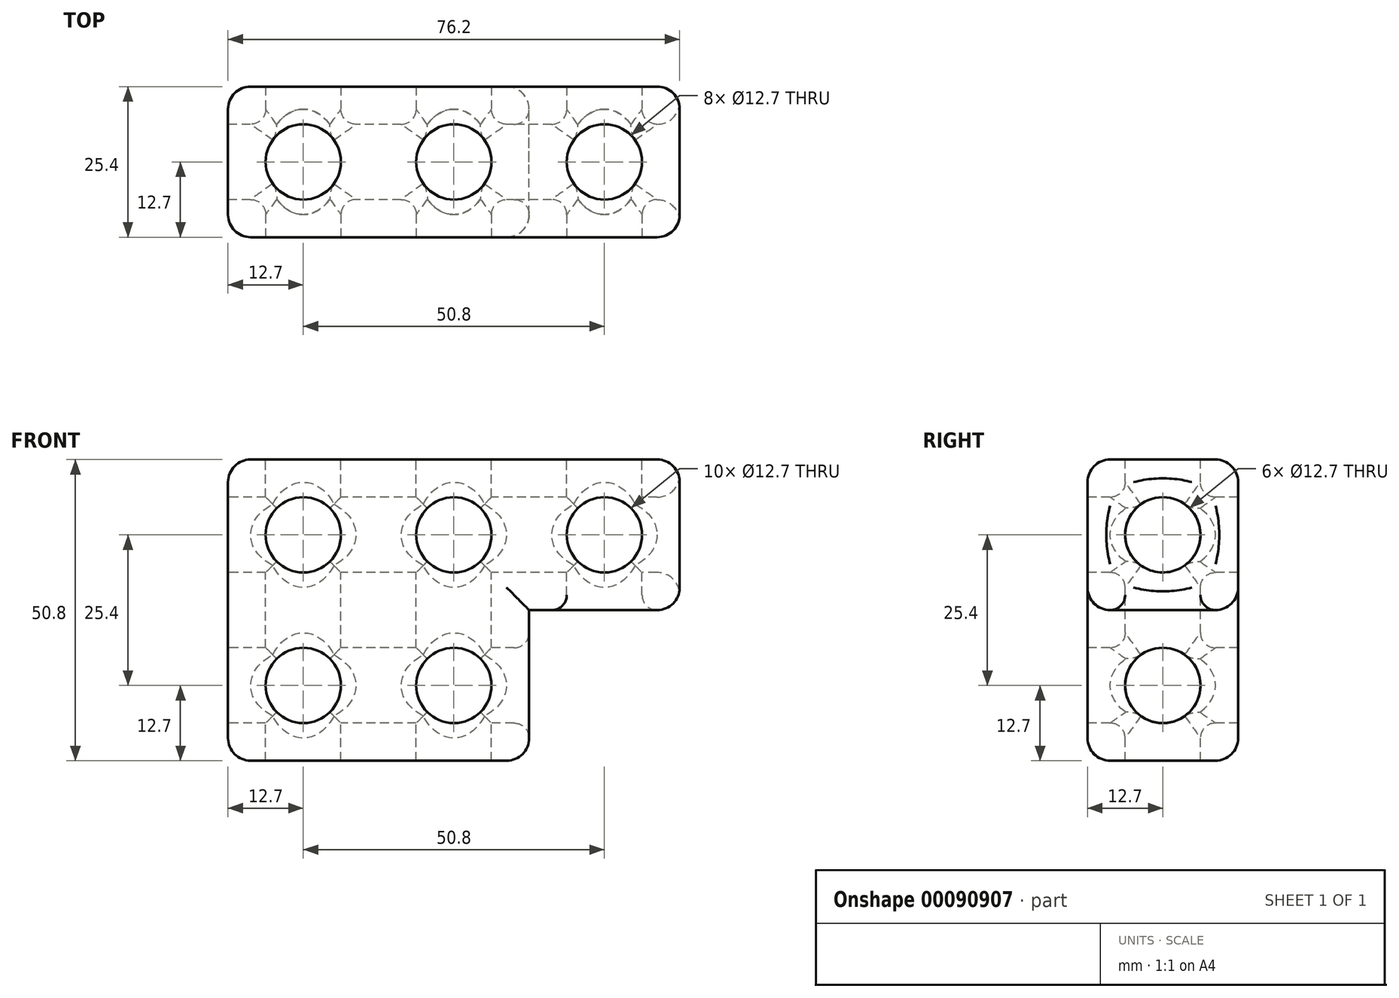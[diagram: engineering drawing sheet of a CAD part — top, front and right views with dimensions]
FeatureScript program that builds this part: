
annotation { "Feature Type Name" : "Feature", "Feature Type Description" : "" }
export const myFeature = defineFeature(function(context is Context, id is Id, definition is map)
    precondition{}
    {
        {
            var Q0;
            Q0=qCreatedBy(makeId("Top.planeOp"),FACE);
            var sketch = newSketch(context, id + "F0", { "sketchPlane" : qUnion([Q0])});
            skLineSegment(sketch, "E0.top", {"start": v(0, 25.4) * mm, "end": v(50.8, 25.4) * mm});
            skLineSegment(sketch, "E0.left", {"start": v(0, 0) * mm, "end": v(0, 25.4) * mm});
            skLineSegment(sketch, "E0.right", {"start": v(50.8, 0) * mm, "end": v(50.8, 25.4) * mm});
            skLineSegment(sketch, "E1", {"start": v(0, 0) * mm, "end": v(50.8, 0) * mm});
            skSolve(sketch);
        }
        {
            var Q0;
            Q0 = qSketchRegion(id + "F0", true);
            extrude(context, id + "F1", {"entities" : qUnion([Q0]), "depth" : 25.4 * mm});
        }
        {
            var Q0;
            Q0=makeQuery(id+"F1.opExtrude","CAP_FACE",FACE,{"disambiguationData":[OSD([sQuery(id+"F0.wireOp",EDGE,"E0.top"),sQuery(id+"F0.wireOp",EDGE,"E0.left"),sQuery(id+"F0.wireOp",EDGE,"E0.right"),sQuery(id+"F0.wireOp",EDGE,"E1")])],"isStart":false});
            var sketch = newSketch(context, id + "F2", { "sketchPlane" : qUnion([Q0])});
            skLineSegment(sketch, "E2.bottom", {"start": v(0, 25.4) * mm, "end": v(76.2, 25.4) * mm});
            skLineSegment(sketch, "E2.top", {"start": v(0, 0) * mm, "end": v(76.2, 0) * mm});
            skLineSegment(sketch, "E2.left", {"start": v(0, 25.4) * mm, "end": v(0, 0) * mm});
            skLineSegment(sketch, "E2.right", {"start": v(76.2, 25.4) * mm, "end": v(76.2, 0) * mm});
            skSolve(sketch);
        }
        {
            var Q0;
            Q0 = qSketchRegion(id + "F2", true);
            extrude(context, id + "F3", {"entities" : qUnion([Q0]), "operationType" : NewBodyOperationType.ADD, "depth" : 25.4 * mm});
        }
        {
            var Q0;
            Q0=makeQuery(id+"F3.boolean.opBoolean","MERGE",FACE,{"derivedFrom":[makeQuery(id+"F1.opExtrude","SWEPT_FACE",FACE,{"disambiguationData":[OSD([sQuery(id+"F0.wireOp",EDGE,"E1")])]}),makeQuery(id+"F3.opExtrude","SWEPT_FACE",FACE,{"disambiguationData":[OSD([sQuery(id+"F2.wireOp",EDGE,"E2.top")])]})]});
            var sketch = newSketch(context, id + "F4", { "sketchPlane" : qUnion([Q0])});
            skCircle(sketch, "E3", {"center": v(12.7, 38.1) * mm, "radius": 6.35 * mm});
            skCircle(sketch, "E4", {"center": v(38.1, 38.1) * mm, "radius": 6.35 * mm});
            skCircle(sketch, "E5", {"center": v(63.5, 38.1) * mm, "radius": 6.35 * mm});
            skCircle(sketch, "E6", {"center": v(38.1, 12.7) * mm, "radius": 6.35 * mm});
            skCircle(sketch, "E7", {"center": v(12.7, 12.7) * mm, "radius": 6.35 * mm});
            skSolve(sketch);
        }
        {
            var Q0;
            Q0 = qSketchRegion(id + "F4", true);
            extrude(context, id + "F5", {"entities" : qUnion([Q0]), "operationType" : NewBodyOperationType.REMOVE, "oppositeDirection" : true, "depth" : 25.4 * mm});
        }
        {
            var Q0;
            Q0=makeQuery(id+"F3.opExtrude","CAP_FACE",FACE,{"disambiguationData":[OSD([sQuery(id+"F2.wireOp",EDGE,"E2.bottom"),sQuery(id+"F2.wireOp",EDGE,"E2.top"),sQuery(id+"F2.wireOp",EDGE,"E2.left"),sQuery(id+"F2.wireOp",EDGE,"E2.right")])],"isStart":false});
            var sketch = newSketch(context, id + "F6", { "sketchPlane" : qUnion([Q0])});
            skCircle(sketch, "E8", {"center": v(12.7, 12.7) * mm, "radius": 6.35 * mm});
            skPoint(sketch, "E8.centerSnap0", {"position": v(0, 12.7) * mm});
            skCircle(sketch, "E9", {"center": v(38.1, 12.7) * mm, "radius": 6.35 * mm});
            skCircle(sketch, "E10", {"center": v(63.5, 12.7) * mm, "radius": 6.35 * mm});
            skSolve(sketch);
        }
        {
            var Q0;
            Q0 = qSketchRegion(id + "F6", true);
            extrude(context, id + "F7", {"entities" : qUnion([Q0]), "operationType" : NewBodyOperationType.REMOVE, "oppositeDirection" : true, "depth" : 50.8 * mm});
        }
        {
            var Q0;
            Q0=makeQuery(id+"F3.boolean.opBoolean","MERGE",FACE,{"derivedFrom":[makeQuery(id+"F1.opExtrude","SWEPT_FACE",FACE,{"disambiguationData":[OSD([sQuery(id+"F0.wireOp",EDGE,"E0.left")])]}),makeQuery(id+"F3.opExtrude","SWEPT_FACE",FACE,{"disambiguationData":[OSD([sQuery(id+"F2.wireOp",EDGE,"E2.left")])]})]});
            var sketch = newSketch(context, id + "F8", { "sketchPlane" : qUnion([Q0])});
            skCircle(sketch, "E11", {"center": v(-12.7, 38.1) * mm, "radius": 6.35 * mm});
            skCircle(sketch, "E12", {"center": v(-12.7, 12.7) * mm, "radius": 6.35 * mm});
            skSolve(sketch);
        }
        {
            var Q0;
            Q0 = qSketchRegion(id + "F8", true);
            extrude(context, id + "F9", {"entities" : qUnion([Q0]), "operationType" : NewBodyOperationType.REMOVE, "oppositeDirection" : true, "depth" : 76.2 * mm});
        }
        {
            var Q0;
            Q0=makeQuery(id+"F7.boolean.opBoolean","COPY",EDGE,{"derivedFrom":makeQuery(id+"F7.opExtrude","CAP_EDGE",EDGE,{"disambiguationData":[OSD([sQuery(id+"F6.wireOp",EDGE,"E8")])],"isStart":false})});
            var Q1;
            Q1=makeQuery(id+"F7.boolean.opBoolean","COPY",EDGE,{"derivedFrom":makeQuery(id+"F7.opExtrude","CAP_EDGE",EDGE,{"disambiguationData":[OSD([sQuery(id+"F6.wireOp",EDGE,"E9")])],"isStart":false})});
            var Q2;
            Q2=makeQuery(id+"F5.boolean.opBoolean","COPY",EDGE,{"derivedFrom":makeQuery(id+"F5.opExtrude","CAP_EDGE",EDGE,{"disambiguationData":[OSD([sQuery(id+"F4.wireOp",EDGE,"E7")])],"isStart":false})});
            var Q3;
            Q3=makeQuery(id+"F9.boolean.opBoolean","COPY",EDGE,{"derivedFrom":makeQuery(id+"F9.opExtrude","CAP_EDGE",EDGE,{"disambiguationData":[OSD([sQuery(id+"F8.wireOp",EDGE,"E11")])],"isStart":true})});
            var Q4;
            Q4=makeQuery(id+"F9.boolean.opBoolean","COPY",EDGE,{"derivedFrom":makeQuery(id+"F9.opExtrude","CAP_EDGE",EDGE,{"disambiguationData":[OSD([sQuery(id+"F8.wireOp",EDGE,"E12")])],"isStart":true})});
            var Q5;
            Q5=makeQuery(id+"F5.boolean.opBoolean","COPY",EDGE,{"derivedFrom":makeQuery(id+"F5.opExtrude","CAP_EDGE",EDGE,{"disambiguationData":[OSD([sQuery(id+"F4.wireOp",EDGE,"E3")])],"isStart":false})});
            var Q6;
            Q6=makeQuery(id+"F5.boolean.opBoolean","COPY",EDGE,{"derivedFrom":makeQuery(id+"F5.opExtrude","CAP_EDGE",EDGE,{"disambiguationData":[OSD([sQuery(id+"F4.wireOp",EDGE,"E4")])],"isStart":false})});
            var Q7;
            Q7=makeQuery(id+"F5.boolean.opBoolean","COPY",EDGE,{"derivedFrom":makeQuery(id+"F5.opExtrude","CAP_EDGE",EDGE,{"disambiguationData":[OSD([sQuery(id+"F4.wireOp",EDGE,"E6")])],"isStart":false})});
            var Q8;
            Q8=makeQuery(id+"F5.boolean.opBoolean","COPY",EDGE,{"derivedFrom":makeQuery(id+"F5.opExtrude","CAP_EDGE",EDGE,{"disambiguationData":[OSD([sQuery(id+"F4.wireOp",EDGE,"E5")])],"isStart":false})});
            var Q9;
            Q9=makeQuery(id+"F7.boolean.opBoolean","INTERSECT",EDGE,{"derivedFrom":[makeQuery(id+"F3.opExtrude","CAP_FACE",FACE,{"disambiguationData":[OSD([sQuery(id+"F2.wireOp",EDGE,"E2.bottom"),sQuery(id+"F2.wireOp",EDGE,"E2.top"),sQuery(id+"F2.wireOp",EDGE,"E2.left"),sQuery(id+"F2.wireOp",EDGE,"E2.right")])],"isStart":true}),makeQuery(id+"F7.opExtrude","SWEPT_FACE",FACE,{"disambiguationData":[OSD([sQuery(id+"F6.wireOp",EDGE,"E10")])]})]});
            var Q10;
            Q10=makeQuery(id+"F9.boolean.opBoolean","COPY",EDGE,{"derivedFrom":makeQuery(id+"F9.opExtrude","CAP_EDGE",EDGE,{"disambiguationData":[OSD([sQuery(id+"F8.wireOp",EDGE,"E11")])],"isStart":false})});
            var Q11;
            Q11=makeQuery(id+"F9.boolean.opBoolean","INTERSECT",EDGE,{"derivedFrom":[makeQuery(id+"F1.opExtrude","SWEPT_FACE",FACE,{"disambiguationData":[OSD([sQuery(id+"F0.wireOp",EDGE,"E0.right")])]}),makeQuery(id+"F9.opExtrude","SWEPT_FACE",FACE,{"disambiguationData":[OSD([sQuery(id+"F8.wireOp",EDGE,"E12")])]})]});
            var Q12;
            Q12=makeQuery(id+"F5.boolean.opBoolean","COPY",EDGE,{"derivedFrom":makeQuery(id+"F5.opExtrude","CAP_EDGE",EDGE,{"disambiguationData":[OSD([sQuery(id+"F4.wireOp",EDGE,"E6")])],"isStart":true})});
            var Q13;
            Q13=makeQuery(id+"F5.boolean.opBoolean","COPY",EDGE,{"derivedFrom":makeQuery(id+"F5.opExtrude","CAP_EDGE",EDGE,{"disambiguationData":[OSD([sQuery(id+"F4.wireOp",EDGE,"E5")])],"isStart":true})});
            var Q14;
            Q14=makeQuery(id+"F5.boolean.opBoolean","COPY",EDGE,{"derivedFrom":makeQuery(id+"F5.opExtrude","CAP_EDGE",EDGE,{"disambiguationData":[OSD([sQuery(id+"F4.wireOp",EDGE,"E4")])],"isStart":true})});
            var Q15;
            Q15=makeQuery(id+"F5.boolean.opBoolean","COPY",EDGE,{"derivedFrom":makeQuery(id+"F5.opExtrude","CAP_EDGE",EDGE,{"disambiguationData":[OSD([sQuery(id+"F4.wireOp",EDGE,"E3")])],"isStart":true})});
            var Q16;
            Q16=makeQuery(id+"F5.boolean.opBoolean","COPY",EDGE,{"derivedFrom":makeQuery(id+"F5.opExtrude","CAP_EDGE",EDGE,{"disambiguationData":[OSD([sQuery(id+"F4.wireOp",EDGE,"E7")])],"isStart":true})});
            var Q17;
            Q17=makeQuery(id+"F7.boolean.opBoolean","COPY",EDGE,{"derivedFrom":makeQuery(id+"F7.opExtrude","CAP_EDGE",EDGE,{"disambiguationData":[OSD([sQuery(id+"F6.wireOp",EDGE,"E8")])],"isStart":true})});
            var Q18;
            Q18=makeQuery(id+"F7.boolean.opBoolean","COPY",EDGE,{"derivedFrom":makeQuery(id+"F7.opExtrude","CAP_EDGE",EDGE,{"disambiguationData":[OSD([sQuery(id+"F6.wireOp",EDGE,"E9")])],"isStart":true})});
            var Q19;
            Q19=makeQuery(id+"F7.boolean.opBoolean","COPY",EDGE,{"derivedFrom":makeQuery(id+"F7.opExtrude","CAP_EDGE",EDGE,{"disambiguationData":[OSD([sQuery(id+"F6.wireOp",EDGE,"E10")])],"isStart":true})});
            fillet(context, id + "F10", {"entities" : qUnion([Q0, Q1, Q2, Q3, Q4, Q5, Q6, Q7, Q8, Q9, Q10, Q11, Q12, Q13, Q14, Q15, Q16, Q17, Q18, Q19]), "radius" : 2.54 * mm, "tangentPropagation" : true, "allowEdgeOverflow" : false});
        }
        {
            var Q0;
            Q0=makeQuery(id+"F3.opExtrude","CAP_EDGE",EDGE,{"disambiguationData":[OSD([sQuery(id+"F2.wireOp",EDGE,"E2.right")])],"isStart":false});
            var Q1;
            Q1=makeQuery(id+"F3.opExtrude","CAP_EDGE",EDGE,{"disambiguationData":[OSD([sQuery(id+"F2.wireOp",EDGE,"E2.bottom")])],"isStart":false});
            var Q2;
            Q2=makeQuery(id+"F3.opExtrude","SWEPT_EDGE",EDGE,{"disambiguationData":[OSD([sQuery(id+"F2.wireOp",EDGE,"E2.bottom"),sQuery(id+"F2.wireOp",EDGE,"E2.right")])]});
            var Q3;
            Q3=makeQuery(id+"F3.opExtrude","CAP_EDGE",EDGE,{"disambiguationData":[OSD([sQuery(id+"F2.wireOp",EDGE,"E2.top")])],"isStart":false});
            var Q4;
            Q4=makeQuery(id+"F3.opExtrude","CAP_EDGE",EDGE,{"disambiguationData":[OSD([sQuery(id+"F2.wireOp",EDGE,"E2.top")])],"isStart":true});
            var Q5;
            Q5=makeQuery(id+"F3.opExtrude","CAP_EDGE",EDGE,{"disambiguationData":[OSD([sQuery(id+"F2.wireOp",EDGE,"E2.right")])],"isStart":true});
            var Q6;
            Q6=makeQuery(id+"F3.opExtrude","SWEPT_FACE",FACE,{"disambiguationData":[OSD([sQuery(id+"F2.wireOp",EDGE,"E2.right")])]});
            var Q7;
            Q7=makeQuery(id+"F3.opExtrude","CAP_EDGE",EDGE,{"disambiguationData":[OSD([sQuery(id+"F2.wireOp",EDGE,"E2.bottom")])],"isStart":true});
            var Q8;
            Q8=makeQuery(id+"F1.opExtrude","SWEPT_EDGE",EDGE,{"disambiguationData":[OSD([sQuery(id+"F0.wireOp",EDGE,"E0.top"),sQuery(id+"F0.wireOp",EDGE,"E0.right")])]});
            var Q9;
            Q9=makeQuery(id+"F1.opExtrude","CAP_EDGE",EDGE,{"disambiguationData":[OSD([sQuery(id+"F0.wireOp",EDGE,"E0.top")])],"isStart":true});
            var Q10;
            Q10=makeQuery(id+"F1.opExtrude","CAP_EDGE",EDGE,{"disambiguationData":[OSD([sQuery(id+"F0.wireOp",EDGE,"E0.right")])],"isStart":true});
            var Q11;
            Q11=makeQuery(id+"F1.opExtrude","CAP_EDGE",EDGE,{"disambiguationData":[OSD([sQuery(id+"F0.wireOp",EDGE,"E1")])],"isStart":true});
            var Q12;
            Q12=makeQuery(id+"F1.opExtrude","SWEPT_EDGE",EDGE,{"disambiguationData":[OSD([sQuery(id+"F0.wireOp",EDGE,"E0.right"),sQuery(id+"F0.wireOp",EDGE,"E1")])]});
            var Q13;
            Q13=makeQuery(id+"F1.opExtrude","CAP_EDGE",EDGE,{"disambiguationData":[OSD([sQuery(id+"F0.wireOp",EDGE,"E0.left")])],"isStart":true});
            var Q14;
            Q14=makeQuery(id+"F3.boolean.opBoolean","MERGE",EDGE,{"derivedFrom":[makeQuery(id+"F1.opExtrude","SWEPT_EDGE",EDGE,{"disambiguationData":[OSD([sQuery(id+"F0.wireOp",EDGE,"E0.top"),sQuery(id+"F0.wireOp",EDGE,"E0.left")])]}),makeQuery(id+"F3.opExtrude","SWEPT_EDGE",EDGE,{"disambiguationData":[OSD([sQuery(id+"F2.wireOp",EDGE,"E2.bottom"),sQuery(id+"F2.wireOp",EDGE,"E2.left")])]})]});
            var Q15;
            Q15=makeQuery(id+"F3.boolean.opBoolean","MERGE",EDGE,{"derivedFrom":[makeQuery(id+"F1.opExtrude","SWEPT_EDGE",EDGE,{"disambiguationData":[OSD([sQuery(id+"F0.wireOp",EDGE,"E0.left"),sQuery(id+"F0.wireOp",EDGE,"E1")])]}),makeQuery(id+"F3.opExtrude","SWEPT_EDGE",EDGE,{"disambiguationData":[OSD([sQuery(id+"F2.wireOp",EDGE,"E2.top"),sQuery(id+"F2.wireOp",EDGE,"E2.left")])]})]});
            var Q16;
            Q16=makeQuery(id+"F3.opExtrude","CAP_EDGE",EDGE,{"disambiguationData":[OSD([sQuery(id+"F2.wireOp",EDGE,"E2.left")])],"isStart":false});
            fillet(context, id + "F11", {"entities" : qUnion([Q0, Q1, Q2, Q3, Q4, Q5, Q6, Q7, Q8, Q9, Q10, Q11, Q12, Q13, Q14, Q15, Q16]), "radius" : 3.8 * mm, "tangentPropagation" : true, "allowEdgeOverflow" : false});
        }
        {
            var Q0;
            Q0=makeQuery(id+"F9.boolean.opBoolean","INTERSECT",EDGE,{"disambiguationData":[OD(0.0)],"derivedFrom":[makeQuery(id+"F7.boolean.opBoolean","COPY",FACE,{"disambiguationData":[OD(1.0)],"derivedFrom":makeQuery(id+"F7.opExtrude","SWEPT_FACE",FACE,{"disambiguationData":[OSD([sQuery(id+"F6.wireOp",EDGE,"E8")])]})}),makeQuery(id+"F9.opExtrude","SWEPT_FACE",FACE,{"disambiguationData":[OSD([sQuery(id+"F8.wireOp",EDGE,"E12")])]})]});
            var Q1;
            Q1=makeQuery(id+"F7.boolean.opBoolean","INTERSECT",EDGE,{"disambiguationData":[OD(0.0)],"derivedFrom":[makeQuery(id+"F5.boolean.opBoolean","COPY",FACE,{"derivedFrom":makeQuery(id+"F5.opExtrude","SWEPT_FACE",FACE,{"disambiguationData":[OSD([sQuery(id+"F4.wireOp",EDGE,"E7")])]})}),makeQuery(id+"F7.opExtrude","SWEPT_FACE",FACE,{"disambiguationData":[OSD([sQuery(id+"F6.wireOp",EDGE,"E8")])]})]});
            var Q2;
            {var subQ0=makeQuery(id+"F5.boolean.opBoolean","COPY",FACE,{"derivedFrom":makeQuery(id+"F5.opExtrude","SWEPT_FACE",FACE,{"disambiguationData":[OSD([sQuery(id+"F4.wireOp",EDGE,"E6")])]})});Q2=makeQuery(id+"F9.boolean.opBoolean","INTERSECT",EDGE,{"disambiguationData":[OD(1.0)],"derivedFrom":[makeQuery(id+"F7.boolean.opBoolean","SPLIT",FACE,{"disambiguationData":[TD([makeQuery(id+"F1.opExtrude","SWEPT_FACE",FACE,{"disambiguationData":[OSD([sQuery(id+"F0.wireOp",EDGE,"E1")])]})])],"derivedFrom":subQ0}),makeQuery(id+"F9.opExtrude","SWEPT_FACE",FACE,{"disambiguationData":[OSD([sQuery(id+"F8.wireOp",EDGE,"E12")])]})]});}
            var Q3;
            Q3=makeQuery(id+"F9.boolean.opBoolean","INTERSECT",EDGE,{"disambiguationData":[OD(1.0)],"derivedFrom":[makeQuery(id+"F7.boolean.opBoolean","COPY",FACE,{"disambiguationData":[OD(1.0)],"derivedFrom":makeQuery(id+"F7.opExtrude","SWEPT_FACE",FACE,{"disambiguationData":[OSD([sQuery(id+"F6.wireOp",EDGE,"E9")])]})}),makeQuery(id+"F9.opExtrude","SWEPT_FACE",FACE,{"disambiguationData":[OSD([sQuery(id+"F8.wireOp",EDGE,"E12")])]})]});
            var Q4;
            Q4=makeQuery(id+"F7.boolean.opBoolean","INTERSECT",EDGE,{"disambiguationData":[OD(0.0)],"derivedFrom":[makeQuery(id+"F5.boolean.opBoolean","COPY",FACE,{"derivedFrom":makeQuery(id+"F5.opExtrude","SWEPT_FACE",FACE,{"disambiguationData":[OSD([sQuery(id+"F4.wireOp",EDGE,"E6")])]})}),makeQuery(id+"F7.opExtrude","SWEPT_FACE",FACE,{"disambiguationData":[OSD([sQuery(id+"F6.wireOp",EDGE,"E9")])]})]});
            var Q5;
            {var subQ0=makeQuery(id+"F5.boolean.opBoolean","COPY",FACE,{"derivedFrom":makeQuery(id+"F5.opExtrude","SWEPT_FACE",FACE,{"disambiguationData":[OSD([sQuery(id+"F4.wireOp",EDGE,"E3")])]})});Q5=makeQuery(id+"F9.boolean.opBoolean","INTERSECT",EDGE,{"disambiguationData":[OD(0.0)],"derivedFrom":[makeQuery(id+"F7.boolean.opBoolean","SPLIT",FACE,{"disambiguationData":[TD([makeQuery(id+"F1.opExtrude","SWEPT_FACE",FACE,{"disambiguationData":[OSD([sQuery(id+"F0.wireOp",EDGE,"E1")])]})])],"derivedFrom":subQ0}),makeQuery(id+"F9.opExtrude","SWEPT_FACE",FACE,{"disambiguationData":[OSD([sQuery(id+"F8.wireOp",EDGE,"E11")])]})]});}
            var Q6;
            Q6=makeQuery(id+"F9.boolean.opBoolean","INTERSECT",EDGE,{"disambiguationData":[OD(0.0)],"derivedFrom":[makeQuery(id+"F7.boolean.opBoolean","COPY",FACE,{"disambiguationData":[OD(2.0)],"derivedFrom":makeQuery(id+"F7.opExtrude","SWEPT_FACE",FACE,{"disambiguationData":[OSD([sQuery(id+"F6.wireOp",EDGE,"E8")])]})}),makeQuery(id+"F9.opExtrude","SWEPT_FACE",FACE,{"disambiguationData":[OSD([sQuery(id+"F8.wireOp",EDGE,"E11")])]})]});
            var Q7;
            Q7=makeQuery(id+"F7.boolean.opBoolean","INTERSECT",EDGE,{"disambiguationData":[OD(1.0)],"derivedFrom":[makeQuery(id+"F5.boolean.opBoolean","COPY",FACE,{"derivedFrom":makeQuery(id+"F5.opExtrude","SWEPT_FACE",FACE,{"disambiguationData":[OSD([sQuery(id+"F4.wireOp",EDGE,"E3")])]})}),makeQuery(id+"F7.opExtrude","SWEPT_FACE",FACE,{"disambiguationData":[OSD([sQuery(id+"F6.wireOp",EDGE,"E8")])]})]});
            var Q8;
            {var subQ0=makeQuery(id+"F5.boolean.opBoolean","COPY",FACE,{"derivedFrom":makeQuery(id+"F5.opExtrude","SWEPT_FACE",FACE,{"disambiguationData":[OSD([sQuery(id+"F4.wireOp",EDGE,"E4")])]})});Q8=makeQuery(id+"F9.boolean.opBoolean","INTERSECT",EDGE,{"disambiguationData":[OD(0.0)],"derivedFrom":[makeQuery(id+"F7.boolean.opBoolean","SPLIT",FACE,{"disambiguationData":[TD([makeQuery(id+"F1.opExtrude","SWEPT_FACE",FACE,{"disambiguationData":[OSD([sQuery(id+"F0.wireOp",EDGE,"E1")])]})])],"derivedFrom":subQ0}),makeQuery(id+"F9.opExtrude","SWEPT_FACE",FACE,{"disambiguationData":[OSD([sQuery(id+"F8.wireOp",EDGE,"E11")])]})]});}
            var Q9;
            Q9=makeQuery(id+"F9.boolean.opBoolean","INTERSECT",EDGE,{"disambiguationData":[OD(0.0)],"derivedFrom":[makeQuery(id+"F7.boolean.opBoolean","COPY",FACE,{"disambiguationData":[OD(2.0)],"derivedFrom":makeQuery(id+"F7.opExtrude","SWEPT_FACE",FACE,{"disambiguationData":[OSD([sQuery(id+"F6.wireOp",EDGE,"E9")])]})}),makeQuery(id+"F9.opExtrude","SWEPT_FACE",FACE,{"disambiguationData":[OSD([sQuery(id+"F8.wireOp",EDGE,"E11")])]})]});
            var Q10;
            Q10=makeQuery(id+"F7.boolean.opBoolean","INTERSECT",EDGE,{"disambiguationData":[OD(1.0)],"derivedFrom":[makeQuery(id+"F5.boolean.opBoolean","COPY",FACE,{"derivedFrom":makeQuery(id+"F5.opExtrude","SWEPT_FACE",FACE,{"disambiguationData":[OSD([sQuery(id+"F4.wireOp",EDGE,"E4")])]})}),makeQuery(id+"F7.opExtrude","SWEPT_FACE",FACE,{"disambiguationData":[OSD([sQuery(id+"F6.wireOp",EDGE,"E9")])]})]});
            var Q11;
            {var subQ0=makeQuery(id+"F5.boolean.opBoolean","COPY",FACE,{"derivedFrom":makeQuery(id+"F5.opExtrude","SWEPT_FACE",FACE,{"disambiguationData":[OSD([sQuery(id+"F4.wireOp",EDGE,"E5")])]})});Q11=makeQuery(id+"F9.boolean.opBoolean","INTERSECT",EDGE,{"disambiguationData":[OD(1.0)],"derivedFrom":[makeQuery(id+"F7.boolean.opBoolean","SPLIT",FACE,{"disambiguationData":[TD([makeQuery(id+"F1.opExtrude","SWEPT_FACE",FACE,{"disambiguationData":[OSD([sQuery(id+"F0.wireOp",EDGE,"E1")])]})])],"derivedFrom":subQ0}),makeQuery(id+"F9.opExtrude","SWEPT_FACE",FACE,{"disambiguationData":[OSD([sQuery(id+"F8.wireOp",EDGE,"E11")])]})]});}
            var Q12;
            Q12=makeQuery(id+"F9.boolean.opBoolean","INTERSECT",EDGE,{"disambiguationData":[OD(1.0)],"derivedFrom":[makeQuery(id+"F7.boolean.opBoolean","COPY",FACE,{"disambiguationData":[OD(1.0)],"derivedFrom":makeQuery(id+"F7.opExtrude","SWEPT_FACE",FACE,{"disambiguationData":[OSD([sQuery(id+"F6.wireOp",EDGE,"E10")])]})}),makeQuery(id+"F9.opExtrude","SWEPT_FACE",FACE,{"disambiguationData":[OSD([sQuery(id+"F8.wireOp",EDGE,"E11")])]})]});
            var Q13;
            Q13=makeQuery(id+"F7.boolean.opBoolean","INTERSECT",EDGE,{"disambiguationData":[OD(1.0)],"derivedFrom":[makeQuery(id+"F5.boolean.opBoolean","COPY",FACE,{"derivedFrom":makeQuery(id+"F5.opExtrude","SWEPT_FACE",FACE,{"disambiguationData":[OSD([sQuery(id+"F4.wireOp",EDGE,"E5")])]})}),makeQuery(id+"F7.opExtrude","SWEPT_FACE",FACE,{"disambiguationData":[OSD([sQuery(id+"F6.wireOp",EDGE,"E10")])]})]});
            var Q14;
            Q14=makeQuery(id+"F9.boolean.opBoolean","INTERSECT",EDGE,{"disambiguationData":[OD(0.0)],"derivedFrom":[makeQuery(id+"F7.boolean.opBoolean","COPY",FACE,{"disambiguationData":[OD(0.0)],"derivedFrom":makeQuery(id+"F7.opExtrude","SWEPT_FACE",FACE,{"disambiguationData":[OSD([sQuery(id+"F6.wireOp",EDGE,"E10")])]})}),makeQuery(id+"F9.opExtrude","SWEPT_FACE",FACE,{"disambiguationData":[OSD([sQuery(id+"F8.wireOp",EDGE,"E11")])]})]});
            var Q15;
            Q15=makeQuery(id+"F7.boolean.opBoolean","INTERSECT",EDGE,{"disambiguationData":[OD(0.0)],"derivedFrom":[makeQuery(id+"F5.boolean.opBoolean","COPY",FACE,{"derivedFrom":makeQuery(id+"F5.opExtrude","SWEPT_FACE",FACE,{"disambiguationData":[OSD([sQuery(id+"F4.wireOp",EDGE,"E5")])]})}),makeQuery(id+"F7.opExtrude","SWEPT_FACE",FACE,{"disambiguationData":[OSD([sQuery(id+"F6.wireOp",EDGE,"E10")])]})]});
            var Q16;
            {var subQ0=makeQuery(id+"F5.boolean.opBoolean","COPY",FACE,{"derivedFrom":makeQuery(id+"F5.opExtrude","SWEPT_FACE",FACE,{"disambiguationData":[OSD([sQuery(id+"F4.wireOp",EDGE,"E5")])]})});Q16=makeQuery(id+"F9.boolean.opBoolean","INTERSECT",EDGE,{"disambiguationData":[OD(0.0)],"derivedFrom":[makeQuery(id+"F7.boolean.opBoolean","SPLIT",FACE,{"disambiguationData":[TD([makeQuery(id+"F1.opExtrude","SWEPT_FACE",FACE,{"disambiguationData":[OSD([sQuery(id+"F0.wireOp",EDGE,"E1")])]})])],"derivedFrom":subQ0}),makeQuery(id+"F9.opExtrude","SWEPT_FACE",FACE,{"disambiguationData":[OSD([sQuery(id+"F8.wireOp",EDGE,"E11")])]})]});}
            var Q17;
            Q17=makeQuery(id+"F9.boolean.opBoolean","INTERSECT",EDGE,{"disambiguationData":[OD(0.0)],"derivedFrom":[makeQuery(id+"F7.boolean.opBoolean","COPY",FACE,{"disambiguationData":[OD(1.0)],"derivedFrom":makeQuery(id+"F7.opExtrude","SWEPT_FACE",FACE,{"disambiguationData":[OSD([sQuery(id+"F6.wireOp",EDGE,"E10")])]})}),makeQuery(id+"F9.opExtrude","SWEPT_FACE",FACE,{"disambiguationData":[OSD([sQuery(id+"F8.wireOp",EDGE,"E11")])]})]});
            var Q18;
            Q18=makeQuery(id+"F9.boolean.opBoolean","INTERSECT",EDGE,{"disambiguationData":[OD(0.0)],"derivedFrom":[makeQuery(id+"F7.boolean.opBoolean","COPY",FACE,{"disambiguationData":[OD(1.0)],"derivedFrom":makeQuery(id+"F7.opExtrude","SWEPT_FACE",FACE,{"disambiguationData":[OSD([sQuery(id+"F6.wireOp",EDGE,"E9")])]})}),makeQuery(id+"F9.opExtrude","SWEPT_FACE",FACE,{"disambiguationData":[OSD([sQuery(id+"F8.wireOp",EDGE,"E12")])]})]});
            var Q19;
            Q19=makeQuery(id+"F9.boolean.opBoolean","INTERSECT",EDGE,{"disambiguationData":[OD(0.0)],"derivedFrom":[makeQuery(id+"F7.boolean.opBoolean","COPY",FACE,{"disambiguationData":[OD(2.0)],"derivedFrom":makeQuery(id+"F7.opExtrude","SWEPT_FACE",FACE,{"disambiguationData":[OSD([sQuery(id+"F6.wireOp",EDGE,"E9")])]})}),makeQuery(id+"F9.opExtrude","SWEPT_FACE",FACE,{"disambiguationData":[OSD([sQuery(id+"F8.wireOp",EDGE,"E12")])]})]});
            var Q20;
            Q20=makeQuery(id+"F7.boolean.opBoolean","INTERSECT",EDGE,{"disambiguationData":[OD(1.0)],"derivedFrom":[makeQuery(id+"F5.boolean.opBoolean","COPY",FACE,{"derivedFrom":makeQuery(id+"F5.opExtrude","SWEPT_FACE",FACE,{"disambiguationData":[OSD([sQuery(id+"F4.wireOp",EDGE,"E6")])]})}),makeQuery(id+"F7.opExtrude","SWEPT_FACE",FACE,{"disambiguationData":[OSD([sQuery(id+"F6.wireOp",EDGE,"E9")])]})]});
            var Q21;
            {var subQ0=makeQuery(id+"F5.boolean.opBoolean","COPY",FACE,{"derivedFrom":makeQuery(id+"F5.opExtrude","SWEPT_FACE",FACE,{"disambiguationData":[OSD([sQuery(id+"F4.wireOp",EDGE,"E6")])]})});Q21=makeQuery(id+"F9.boolean.opBoolean","INTERSECT",EDGE,{"disambiguationData":[OD(0.0)],"derivedFrom":[makeQuery(id+"F7.boolean.opBoolean","SPLIT",FACE,{"disambiguationData":[TD([makeQuery(id+"F1.opExtrude","SWEPT_FACE",FACE,{"disambiguationData":[OSD([sQuery(id+"F0.wireOp",EDGE,"E1")])]})])],"derivedFrom":subQ0}),makeQuery(id+"F9.opExtrude","SWEPT_FACE",FACE,{"disambiguationData":[OSD([sQuery(id+"F8.wireOp",EDGE,"E12")])]})]});}
            var Q22;
            Q22=makeQuery(id+"F9.boolean.opBoolean","INTERSECT",EDGE,{"disambiguationData":[OD(1.0)],"derivedFrom":[makeQuery(id+"F7.boolean.opBoolean","COPY",FACE,{"disambiguationData":[OD(1.0)],"derivedFrom":makeQuery(id+"F7.opExtrude","SWEPT_FACE",FACE,{"disambiguationData":[OSD([sQuery(id+"F6.wireOp",EDGE,"E8")])]})}),makeQuery(id+"F9.opExtrude","SWEPT_FACE",FACE,{"disambiguationData":[OSD([sQuery(id+"F8.wireOp",EDGE,"E12")])]})]});
            var Q23;
            Q23=makeQuery(id+"F9.boolean.opBoolean","INTERSECT",EDGE,{"disambiguationData":[OD(1.0)],"derivedFrom":[makeQuery(id+"F7.boolean.opBoolean","COPY",FACE,{"disambiguationData":[OD(2.0)],"derivedFrom":makeQuery(id+"F7.opExtrude","SWEPT_FACE",FACE,{"disambiguationData":[OSD([sQuery(id+"F6.wireOp",EDGE,"E8")])]})}),makeQuery(id+"F9.opExtrude","SWEPT_FACE",FACE,{"disambiguationData":[OSD([sQuery(id+"F8.wireOp",EDGE,"E12")])]})]});
            var Q24;
            Q24=makeQuery(id+"F7.boolean.opBoolean","INTERSECT",EDGE,{"disambiguationData":[OD(1.0)],"derivedFrom":[makeQuery(id+"F5.boolean.opBoolean","COPY",FACE,{"derivedFrom":makeQuery(id+"F5.opExtrude","SWEPT_FACE",FACE,{"disambiguationData":[OSD([sQuery(id+"F4.wireOp",EDGE,"E7")])]})}),makeQuery(id+"F7.opExtrude","SWEPT_FACE",FACE,{"disambiguationData":[OSD([sQuery(id+"F6.wireOp",EDGE,"E8")])]})]});
            var Q25;
            {var subQ0=makeQuery(id+"F5.boolean.opBoolean","COPY",FACE,{"derivedFrom":makeQuery(id+"F5.opExtrude","SWEPT_FACE",FACE,{"disambiguationData":[OSD([sQuery(id+"F4.wireOp",EDGE,"E7")])]})});Q25=makeQuery(id+"F9.boolean.opBoolean","INTERSECT",EDGE,{"disambiguationData":[OD(1.0)],"derivedFrom":[makeQuery(id+"F7.boolean.opBoolean","SPLIT",FACE,{"disambiguationData":[TD([makeQuery(id+"F1.opExtrude","SWEPT_FACE",FACE,{"disambiguationData":[OSD([sQuery(id+"F0.wireOp",EDGE,"E1")])]})])],"derivedFrom":subQ0}),makeQuery(id+"F9.opExtrude","SWEPT_FACE",FACE,{"disambiguationData":[OSD([sQuery(id+"F8.wireOp",EDGE,"E12")])]})]});}
            var Q26;
            {var subQ0=makeQuery(id+"F5.boolean.opBoolean","COPY",FACE,{"derivedFrom":makeQuery(id+"F5.opExtrude","SWEPT_FACE",FACE,{"disambiguationData":[OSD([sQuery(id+"F4.wireOp",EDGE,"E7")])]})});Q26=makeQuery(id+"F9.boolean.opBoolean","INTERSECT",EDGE,{"disambiguationData":[OD(1.0)],"derivedFrom":[makeQuery(id+"F7.boolean.opBoolean","SPLIT",FACE,{"disambiguationData":[TD([makeQuery(id+"F1.opExtrude","SWEPT_FACE",FACE,{"disambiguationData":[OSD([sQuery(id+"F0.wireOp",EDGE,"E0.top")])]})])],"derivedFrom":subQ0}),makeQuery(id+"F9.opExtrude","SWEPT_FACE",FACE,{"disambiguationData":[OSD([sQuery(id+"F8.wireOp",EDGE,"E12")])]})]});}
            var Q27;
            Q27=makeQuery(id+"F7.boolean.opBoolean","INTERSECT",EDGE,{"disambiguationData":[OD(2.0)],"derivedFrom":[makeQuery(id+"F5.boolean.opBoolean","COPY",FACE,{"derivedFrom":makeQuery(id+"F5.opExtrude","SWEPT_FACE",FACE,{"disambiguationData":[OSD([sQuery(id+"F4.wireOp",EDGE,"E7")])]})}),makeQuery(id+"F7.opExtrude","SWEPT_FACE",FACE,{"disambiguationData":[OSD([sQuery(id+"F6.wireOp",EDGE,"E8")])]})]});
            var Q28;
            Q28=makeQuery(id+"F7.boolean.opBoolean","INTERSECT",EDGE,{"disambiguationData":[OD(3.0)],"derivedFrom":[makeQuery(id+"F5.boolean.opBoolean","COPY",FACE,{"derivedFrom":makeQuery(id+"F5.opExtrude","SWEPT_FACE",FACE,{"disambiguationData":[OSD([sQuery(id+"F4.wireOp",EDGE,"E3")])]})}),makeQuery(id+"F7.opExtrude","SWEPT_FACE",FACE,{"disambiguationData":[OSD([sQuery(id+"F6.wireOp",EDGE,"E8")])]})]});
            var Q29;
            {var subQ0=makeQuery(id+"F5.boolean.opBoolean","COPY",FACE,{"derivedFrom":makeQuery(id+"F5.opExtrude","SWEPT_FACE",FACE,{"disambiguationData":[OSD([sQuery(id+"F4.wireOp",EDGE,"E3")])]})});Q29=makeQuery(id+"F9.boolean.opBoolean","INTERSECT",EDGE,{"disambiguationData":[OD(1.0)],"derivedFrom":[makeQuery(id+"F7.boolean.opBoolean","SPLIT",FACE,{"disambiguationData":[TD([makeQuery(id+"F1.opExtrude","SWEPT_FACE",FACE,{"disambiguationData":[OSD([sQuery(id+"F0.wireOp",EDGE,"E0.top")])]})])],"derivedFrom":subQ0}),makeQuery(id+"F9.opExtrude","SWEPT_FACE",FACE,{"disambiguationData":[OSD([sQuery(id+"F8.wireOp",EDGE,"E11")])]})]});}
            var Q30;
            Q30=makeQuery(id+"F9.boolean.opBoolean","INTERSECT",EDGE,{"disambiguationData":[OD(1.0)],"derivedFrom":[makeQuery(id+"F7.boolean.opBoolean","COPY",FACE,{"disambiguationData":[OD(2.0)],"derivedFrom":makeQuery(id+"F7.opExtrude","SWEPT_FACE",FACE,{"disambiguationData":[OSD([sQuery(id+"F6.wireOp",EDGE,"E8")])]})}),makeQuery(id+"F9.opExtrude","SWEPT_FACE",FACE,{"disambiguationData":[OSD([sQuery(id+"F8.wireOp",EDGE,"E11")])]})]});
            var Q31;
            {var subQ0=makeQuery(id+"F5.boolean.opBoolean","COPY",FACE,{"derivedFrom":makeQuery(id+"F5.opExtrude","SWEPT_FACE",FACE,{"disambiguationData":[OSD([sQuery(id+"F4.wireOp",EDGE,"E4")])]})});Q31=makeQuery(id+"F9.boolean.opBoolean","INTERSECT",EDGE,{"disambiguationData":[OD(1.0)],"derivedFrom":[makeQuery(id+"F7.boolean.opBoolean","SPLIT",FACE,{"disambiguationData":[TD([makeQuery(id+"F1.opExtrude","SWEPT_FACE",FACE,{"disambiguationData":[OSD([sQuery(id+"F0.wireOp",EDGE,"E0.top")])]})])],"derivedFrom":subQ0}),makeQuery(id+"F9.opExtrude","SWEPT_FACE",FACE,{"disambiguationData":[OSD([sQuery(id+"F8.wireOp",EDGE,"E11")])]})]});}
            var Q32;
            Q32=makeQuery(id+"F7.boolean.opBoolean","INTERSECT",EDGE,{"disambiguationData":[OD(3.0)],"derivedFrom":[makeQuery(id+"F5.boolean.opBoolean","COPY",FACE,{"derivedFrom":makeQuery(id+"F5.opExtrude","SWEPT_FACE",FACE,{"disambiguationData":[OSD([sQuery(id+"F4.wireOp",EDGE,"E4")])]})}),makeQuery(id+"F7.opExtrude","SWEPT_FACE",FACE,{"disambiguationData":[OSD([sQuery(id+"F6.wireOp",EDGE,"E9")])]})]});
            var Q33;
            Q33=makeQuery(id+"F9.boolean.opBoolean","INTERSECT",EDGE,{"disambiguationData":[OD(1.0)],"derivedFrom":[makeQuery(id+"F7.boolean.opBoolean","COPY",FACE,{"disambiguationData":[OD(2.0)],"derivedFrom":makeQuery(id+"F7.opExtrude","SWEPT_FACE",FACE,{"disambiguationData":[OSD([sQuery(id+"F6.wireOp",EDGE,"E9")])]})}),makeQuery(id+"F9.opExtrude","SWEPT_FACE",FACE,{"disambiguationData":[OSD([sQuery(id+"F8.wireOp",EDGE,"E11")])]})]});
            var Q34;
            {var subQ0=makeQuery(id+"F5.boolean.opBoolean","COPY",FACE,{"derivedFrom":makeQuery(id+"F5.opExtrude","SWEPT_FACE",FACE,{"disambiguationData":[OSD([sQuery(id+"F4.wireOp",EDGE,"E6")])]})});Q34=makeQuery(id+"F9.boolean.opBoolean","INTERSECT",EDGE,{"disambiguationData":[OD(0.0)],"derivedFrom":[makeQuery(id+"F7.boolean.opBoolean","SPLIT",FACE,{"disambiguationData":[TD([makeQuery(id+"F1.opExtrude","SWEPT_FACE",FACE,{"disambiguationData":[OSD([sQuery(id+"F0.wireOp",EDGE,"E0.top")])]})])],"derivedFrom":subQ0}),makeQuery(id+"F9.opExtrude","SWEPT_FACE",FACE,{"disambiguationData":[OSD([sQuery(id+"F8.wireOp",EDGE,"E12")])]})]});}
            var Q35;
            Q35=makeQuery(id+"F7.boolean.opBoolean","INTERSECT",EDGE,{"disambiguationData":[OD(2.0)],"derivedFrom":[makeQuery(id+"F5.boolean.opBoolean","COPY",FACE,{"derivedFrom":makeQuery(id+"F5.opExtrude","SWEPT_FACE",FACE,{"disambiguationData":[OSD([sQuery(id+"F4.wireOp",EDGE,"E6")])]})}),makeQuery(id+"F7.opExtrude","SWEPT_FACE",FACE,{"disambiguationData":[OSD([sQuery(id+"F6.wireOp",EDGE,"E9")])]})]});
            var Q36;
            {var subQ0=makeQuery(id+"F5.boolean.opBoolean","COPY",FACE,{"derivedFrom":makeQuery(id+"F5.opExtrude","SWEPT_FACE",FACE,{"disambiguationData":[OSD([sQuery(id+"F4.wireOp",EDGE,"E7")])]})});Q36=makeQuery(id+"F9.boolean.opBoolean","INTERSECT",EDGE,{"disambiguationData":[OD(0.0)],"derivedFrom":[makeQuery(id+"F7.boolean.opBoolean","SPLIT",FACE,{"disambiguationData":[TD([makeQuery(id+"F1.opExtrude","SWEPT_FACE",FACE,{"disambiguationData":[OSD([sQuery(id+"F0.wireOp",EDGE,"E1")])]})])],"derivedFrom":subQ0}),makeQuery(id+"F9.opExtrude","SWEPT_FACE",FACE,{"disambiguationData":[OSD([sQuery(id+"F8.wireOp",EDGE,"E12")])]})]});}
            var Q37;
            {var subQ0=makeQuery(id+"F5.boolean.opBoolean","COPY",FACE,{"derivedFrom":makeQuery(id+"F5.opExtrude","SWEPT_FACE",FACE,{"disambiguationData":[OSD([sQuery(id+"F4.wireOp",EDGE,"E7")])]})});Q37=makeQuery(id+"F9.boolean.opBoolean","INTERSECT",EDGE,{"disambiguationData":[OD(0.0)],"derivedFrom":[makeQuery(id+"F7.boolean.opBoolean","SPLIT",FACE,{"disambiguationData":[TD([makeQuery(id+"F1.opExtrude","SWEPT_FACE",FACE,{"disambiguationData":[OSD([sQuery(id+"F0.wireOp",EDGE,"E0.top")])]})])],"derivedFrom":subQ0}),makeQuery(id+"F9.opExtrude","SWEPT_FACE",FACE,{"disambiguationData":[OSD([sQuery(id+"F8.wireOp",EDGE,"E12")])]})]});}
            var Q38;
            Q38=makeQuery(id+"F7.boolean.opBoolean","INTERSECT",EDGE,{"disambiguationData":[OD(3.0)],"derivedFrom":[makeQuery(id+"F5.boolean.opBoolean","COPY",FACE,{"derivedFrom":makeQuery(id+"F5.opExtrude","SWEPT_FACE",FACE,{"disambiguationData":[OSD([sQuery(id+"F4.wireOp",EDGE,"E7")])]})}),makeQuery(id+"F7.opExtrude","SWEPT_FACE",FACE,{"disambiguationData":[OSD([sQuery(id+"F6.wireOp",EDGE,"E8")])]})]});
            var Q39;
            Q39=makeQuery(id+"F7.boolean.opBoolean","INTERSECT",EDGE,{"disambiguationData":[OD(3.0)],"derivedFrom":[makeQuery(id+"F5.boolean.opBoolean","COPY",FACE,{"derivedFrom":makeQuery(id+"F5.opExtrude","SWEPT_FACE",FACE,{"disambiguationData":[OSD([sQuery(id+"F4.wireOp",EDGE,"E6")])]})}),makeQuery(id+"F7.opExtrude","SWEPT_FACE",FACE,{"disambiguationData":[OSD([sQuery(id+"F6.wireOp",EDGE,"E9")])]})]});
            var Q40;
            {var subQ0=makeQuery(id+"F5.boolean.opBoolean","COPY",FACE,{"derivedFrom":makeQuery(id+"F5.opExtrude","SWEPT_FACE",FACE,{"disambiguationData":[OSD([sQuery(id+"F4.wireOp",EDGE,"E6")])]})});Q40=makeQuery(id+"F9.boolean.opBoolean","INTERSECT",EDGE,{"disambiguationData":[OD(1.0)],"derivedFrom":[makeQuery(id+"F7.boolean.opBoolean","SPLIT",FACE,{"disambiguationData":[TD([makeQuery(id+"F1.opExtrude","SWEPT_FACE",FACE,{"disambiguationData":[OSD([sQuery(id+"F0.wireOp",EDGE,"E0.top")])]})])],"derivedFrom":subQ0}),makeQuery(id+"F9.opExtrude","SWEPT_FACE",FACE,{"disambiguationData":[OSD([sQuery(id+"F8.wireOp",EDGE,"E12")])]})]});}
            var Q41;
            Q41=makeQuery(id+"F9.boolean.opBoolean","INTERSECT",EDGE,{"disambiguationData":[OD(1.0)],"derivedFrom":[makeQuery(id+"F7.boolean.opBoolean","COPY",FACE,{"disambiguationData":[OD(2.0)],"derivedFrom":makeQuery(id+"F7.opExtrude","SWEPT_FACE",FACE,{"disambiguationData":[OSD([sQuery(id+"F6.wireOp",EDGE,"E9")])]})}),makeQuery(id+"F9.opExtrude","SWEPT_FACE",FACE,{"disambiguationData":[OSD([sQuery(id+"F8.wireOp",EDGE,"E12")])]})]});
            var Q42;
            Q42=makeQuery(id+"F9.boolean.opBoolean","INTERSECT",EDGE,{"disambiguationData":[OD(0.0)],"derivedFrom":[makeQuery(id+"F7.boolean.opBoolean","COPY",FACE,{"disambiguationData":[OD(2.0)],"derivedFrom":makeQuery(id+"F7.opExtrude","SWEPT_FACE",FACE,{"disambiguationData":[OSD([sQuery(id+"F6.wireOp",EDGE,"E8")])]})}),makeQuery(id+"F9.opExtrude","SWEPT_FACE",FACE,{"disambiguationData":[OSD([sQuery(id+"F8.wireOp",EDGE,"E12")])]})]});
            var Q43;
            Q43=makeQuery(id+"F9.boolean.opBoolean","INTERSECT",EDGE,{"disambiguationData":[OD(0.0)],"derivedFrom":[makeQuery(id+"F7.boolean.opBoolean","COPY",FACE,{"disambiguationData":[OD(0.0)],"derivedFrom":makeQuery(id+"F7.opExtrude","SWEPT_FACE",FACE,{"disambiguationData":[OSD([sQuery(id+"F6.wireOp",EDGE,"E8")])]})}),makeQuery(id+"F9.opExtrude","SWEPT_FACE",FACE,{"disambiguationData":[OSD([sQuery(id+"F8.wireOp",EDGE,"E11")])]})]});
            var Q44;
            Q44=makeQuery(id+"F7.boolean.opBoolean","INTERSECT",EDGE,{"disambiguationData":[OD(2.0)],"derivedFrom":[makeQuery(id+"F5.boolean.opBoolean","COPY",FACE,{"derivedFrom":makeQuery(id+"F5.opExtrude","SWEPT_FACE",FACE,{"disambiguationData":[OSD([sQuery(id+"F4.wireOp",EDGE,"E3")])]})}),makeQuery(id+"F7.opExtrude","SWEPT_FACE",FACE,{"disambiguationData":[OSD([sQuery(id+"F6.wireOp",EDGE,"E8")])]})]});
            var Q45;
            {var subQ0=makeQuery(id+"F5.boolean.opBoolean","COPY",FACE,{"derivedFrom":makeQuery(id+"F5.opExtrude","SWEPT_FACE",FACE,{"disambiguationData":[OSD([sQuery(id+"F4.wireOp",EDGE,"E3")])]})});Q45=makeQuery(id+"F9.boolean.opBoolean","INTERSECT",EDGE,{"disambiguationData":[OD(0.0)],"derivedFrom":[makeQuery(id+"F7.boolean.opBoolean","SPLIT",FACE,{"disambiguationData":[TD([makeQuery(id+"F1.opExtrude","SWEPT_FACE",FACE,{"disambiguationData":[OSD([sQuery(id+"F0.wireOp",EDGE,"E0.top")])]})])],"derivedFrom":subQ0}),makeQuery(id+"F9.opExtrude","SWEPT_FACE",FACE,{"disambiguationData":[OSD([sQuery(id+"F8.wireOp",EDGE,"E11")])]})]});}
            var Q46;
            Q46=makeQuery(id+"F7.boolean.opBoolean","INTERSECT",EDGE,{"disambiguationData":[OD(0.0)],"derivedFrom":[makeQuery(id+"F5.boolean.opBoolean","COPY",FACE,{"derivedFrom":makeQuery(id+"F5.opExtrude","SWEPT_FACE",FACE,{"disambiguationData":[OSD([sQuery(id+"F4.wireOp",EDGE,"E3")])]})}),makeQuery(id+"F7.opExtrude","SWEPT_FACE",FACE,{"disambiguationData":[OSD([sQuery(id+"F6.wireOp",EDGE,"E8")])]})]});
            var Q47;
            {var subQ0=makeQuery(id+"F5.boolean.opBoolean","COPY",FACE,{"derivedFrom":makeQuery(id+"F5.opExtrude","SWEPT_FACE",FACE,{"disambiguationData":[OSD([sQuery(id+"F4.wireOp",EDGE,"E3")])]})});Q47=makeQuery(id+"F9.boolean.opBoolean","INTERSECT",EDGE,{"disambiguationData":[OD(1.0)],"derivedFrom":[makeQuery(id+"F7.boolean.opBoolean","SPLIT",FACE,{"disambiguationData":[TD([makeQuery(id+"F1.opExtrude","SWEPT_FACE",FACE,{"disambiguationData":[OSD([sQuery(id+"F0.wireOp",EDGE,"E1")])]})])],"derivedFrom":subQ0}),makeQuery(id+"F9.opExtrude","SWEPT_FACE",FACE,{"disambiguationData":[OSD([sQuery(id+"F8.wireOp",EDGE,"E11")])]})]});}
            var Q48;
            Q48=makeQuery(id+"F9.boolean.opBoolean","INTERSECT",EDGE,{"disambiguationData":[OD(1.0)],"derivedFrom":[makeQuery(id+"F7.boolean.opBoolean","COPY",FACE,{"disambiguationData":[OD(0.0)],"derivedFrom":makeQuery(id+"F7.opExtrude","SWEPT_FACE",FACE,{"disambiguationData":[OSD([sQuery(id+"F6.wireOp",EDGE,"E8")])]})}),makeQuery(id+"F9.opExtrude","SWEPT_FACE",FACE,{"disambiguationData":[OSD([sQuery(id+"F8.wireOp",EDGE,"E11")])]})]});
            var Q49;
            Q49=makeQuery(id+"F9.boolean.opBoolean","INTERSECT",EDGE,{"disambiguationData":[OD(1.0)],"derivedFrom":[makeQuery(id+"F7.boolean.opBoolean","COPY",FACE,{"disambiguationData":[OD(0.0)],"derivedFrom":makeQuery(id+"F7.opExtrude","SWEPT_FACE",FACE,{"disambiguationData":[OSD([sQuery(id+"F6.wireOp",EDGE,"E9")])]})}),makeQuery(id+"F9.opExtrude","SWEPT_FACE",FACE,{"disambiguationData":[OSD([sQuery(id+"F8.wireOp",EDGE,"E11")])]})]});
            var Q50;
            {var subQ0=makeQuery(id+"F5.boolean.opBoolean","COPY",FACE,{"derivedFrom":makeQuery(id+"F5.opExtrude","SWEPT_FACE",FACE,{"disambiguationData":[OSD([sQuery(id+"F4.wireOp",EDGE,"E4")])]})});Q50=makeQuery(id+"F9.boolean.opBoolean","INTERSECT",EDGE,{"disambiguationData":[OD(1.0)],"derivedFrom":[makeQuery(id+"F7.boolean.opBoolean","SPLIT",FACE,{"disambiguationData":[TD([makeQuery(id+"F1.opExtrude","SWEPT_FACE",FACE,{"disambiguationData":[OSD([sQuery(id+"F0.wireOp",EDGE,"E1")])]})])],"derivedFrom":subQ0}),makeQuery(id+"F9.opExtrude","SWEPT_FACE",FACE,{"disambiguationData":[OSD([sQuery(id+"F8.wireOp",EDGE,"E11")])]})]});}
            var Q51;
            Q51=makeQuery(id+"F7.boolean.opBoolean","INTERSECT",EDGE,{"disambiguationData":[OD(0.0)],"derivedFrom":[makeQuery(id+"F5.boolean.opBoolean","COPY",FACE,{"derivedFrom":makeQuery(id+"F5.opExtrude","SWEPT_FACE",FACE,{"disambiguationData":[OSD([sQuery(id+"F4.wireOp",EDGE,"E4")])]})}),makeQuery(id+"F7.opExtrude","SWEPT_FACE",FACE,{"disambiguationData":[OSD([sQuery(id+"F6.wireOp",EDGE,"E9")])]})]});
            var Q52;
            Q52=makeQuery(id+"F7.boolean.opBoolean","INTERSECT",EDGE,{"disambiguationData":[OD(2.0)],"derivedFrom":[makeQuery(id+"F5.boolean.opBoolean","COPY",FACE,{"derivedFrom":makeQuery(id+"F5.opExtrude","SWEPT_FACE",FACE,{"disambiguationData":[OSD([sQuery(id+"F4.wireOp",EDGE,"E4")])]})}),makeQuery(id+"F7.opExtrude","SWEPT_FACE",FACE,{"disambiguationData":[OSD([sQuery(id+"F6.wireOp",EDGE,"E9")])]})]});
            var Q53;
            {var subQ0=makeQuery(id+"F5.boolean.opBoolean","COPY",FACE,{"derivedFrom":makeQuery(id+"F5.opExtrude","SWEPT_FACE",FACE,{"disambiguationData":[OSD([sQuery(id+"F4.wireOp",EDGE,"E4")])]})});Q53=makeQuery(id+"F9.boolean.opBoolean","INTERSECT",EDGE,{"disambiguationData":[OD(0.0)],"derivedFrom":[makeQuery(id+"F7.boolean.opBoolean","SPLIT",FACE,{"disambiguationData":[TD([makeQuery(id+"F1.opExtrude","SWEPT_FACE",FACE,{"disambiguationData":[OSD([sQuery(id+"F0.wireOp",EDGE,"E0.top")])]})])],"derivedFrom":subQ0}),makeQuery(id+"F9.opExtrude","SWEPT_FACE",FACE,{"disambiguationData":[OSD([sQuery(id+"F8.wireOp",EDGE,"E11")])]})]});}
            var Q54;
            Q54=makeQuery(id+"F9.boolean.opBoolean","INTERSECT",EDGE,{"disambiguationData":[OD(0.0)],"derivedFrom":[makeQuery(id+"F7.boolean.opBoolean","COPY",FACE,{"disambiguationData":[OD(0.0)],"derivedFrom":makeQuery(id+"F7.opExtrude","SWEPT_FACE",FACE,{"disambiguationData":[OSD([sQuery(id+"F6.wireOp",EDGE,"E9")])]})}),makeQuery(id+"F9.opExtrude","SWEPT_FACE",FACE,{"disambiguationData":[OSD([sQuery(id+"F8.wireOp",EDGE,"E11")])]})]});
            var Q55;
            Q55=makeQuery(id+"F9.boolean.opBoolean","INTERSECT",EDGE,{"disambiguationData":[OD(1.0)],"derivedFrom":[makeQuery(id+"F7.boolean.opBoolean","COPY",FACE,{"disambiguationData":[OD(0.0)],"derivedFrom":makeQuery(id+"F7.opExtrude","SWEPT_FACE",FACE,{"disambiguationData":[OSD([sQuery(id+"F6.wireOp",EDGE,"E10")])]})}),makeQuery(id+"F9.opExtrude","SWEPT_FACE",FACE,{"disambiguationData":[OSD([sQuery(id+"F8.wireOp",EDGE,"E11")])]})]});
            var Q56;
            Q56=makeQuery(id+"F7.boolean.opBoolean","INTERSECT",EDGE,{"disambiguationData":[OD(2.0)],"derivedFrom":[makeQuery(id+"F5.boolean.opBoolean","COPY",FACE,{"derivedFrom":makeQuery(id+"F5.opExtrude","SWEPT_FACE",FACE,{"disambiguationData":[OSD([sQuery(id+"F4.wireOp",EDGE,"E5")])]})}),makeQuery(id+"F7.opExtrude","SWEPT_FACE",FACE,{"disambiguationData":[OSD([sQuery(id+"F6.wireOp",EDGE,"E10")])]})]});
            var Q57;
            {var subQ0=makeQuery(id+"F5.boolean.opBoolean","COPY",FACE,{"derivedFrom":makeQuery(id+"F5.opExtrude","SWEPT_FACE",FACE,{"disambiguationData":[OSD([sQuery(id+"F4.wireOp",EDGE,"E5")])]})});Q57=makeQuery(id+"F9.boolean.opBoolean","INTERSECT",EDGE,{"disambiguationData":[OD(1.0)],"derivedFrom":[makeQuery(id+"F7.boolean.opBoolean","SPLIT",FACE,{"disambiguationData":[TD([makeQuery(id+"F1.opExtrude","SWEPT_FACE",FACE,{"disambiguationData":[OSD([sQuery(id+"F0.wireOp",EDGE,"E0.top")])]})])],"derivedFrom":subQ0}),makeQuery(id+"F9.opExtrude","SWEPT_FACE",FACE,{"disambiguationData":[OSD([sQuery(id+"F8.wireOp",EDGE,"E11")])]})]});}
            var Q58;
            Q58=makeQuery(id+"F7.boolean.opBoolean","INTERSECT",EDGE,{"disambiguationData":[OD(3.0)],"derivedFrom":[makeQuery(id+"F5.boolean.opBoolean","COPY",FACE,{"derivedFrom":makeQuery(id+"F5.opExtrude","SWEPT_FACE",FACE,{"disambiguationData":[OSD([sQuery(id+"F4.wireOp",EDGE,"E5")])]})}),makeQuery(id+"F7.opExtrude","SWEPT_FACE",FACE,{"disambiguationData":[OSD([sQuery(id+"F6.wireOp",EDGE,"E10")])]})]});
            var Q59;
            {var subQ0=makeQuery(id+"F5.boolean.opBoolean","COPY",FACE,{"derivedFrom":makeQuery(id+"F5.opExtrude","SWEPT_FACE",FACE,{"disambiguationData":[OSD([sQuery(id+"F4.wireOp",EDGE,"E5")])]})});Q59=makeQuery(id+"F9.boolean.opBoolean","INTERSECT",EDGE,{"disambiguationData":[OD(0.0)],"derivedFrom":[makeQuery(id+"F7.boolean.opBoolean","SPLIT",FACE,{"disambiguationData":[TD([makeQuery(id+"F1.opExtrude","SWEPT_FACE",FACE,{"disambiguationData":[OSD([sQuery(id+"F0.wireOp",EDGE,"E0.top")])]})])],"derivedFrom":subQ0}),makeQuery(id+"F9.opExtrude","SWEPT_FACE",FACE,{"disambiguationData":[OSD([sQuery(id+"F8.wireOp",EDGE,"E11")])]})]});}
            fillet(context, id + "F12", {"entities" : qUnion([Q0, Q1, Q2, Q3, Q4, Q5, Q6, Q7, Q8, Q9, Q10, Q11, Q12, Q13, Q14, Q15, Q16, Q17, Q18, Q19, Q20, Q21, Q22, Q23, Q24, Q25, Q26, Q27, Q28, Q29, Q30, Q31, Q32, Q33, Q34, Q35, Q36, Q37, Q38, Q39, Q40, Q41, Q42, Q43, Q44, Q45, Q46, Q47, Q48, Q49, Q50, Q51, Q52, Q53, Q54, Q55, Q56, Q57, Q58, Q59]), "radius" : 2.54 * mm, "tangentPropagation" : true, "allowEdgeOverflow" : false});
        }
    });
